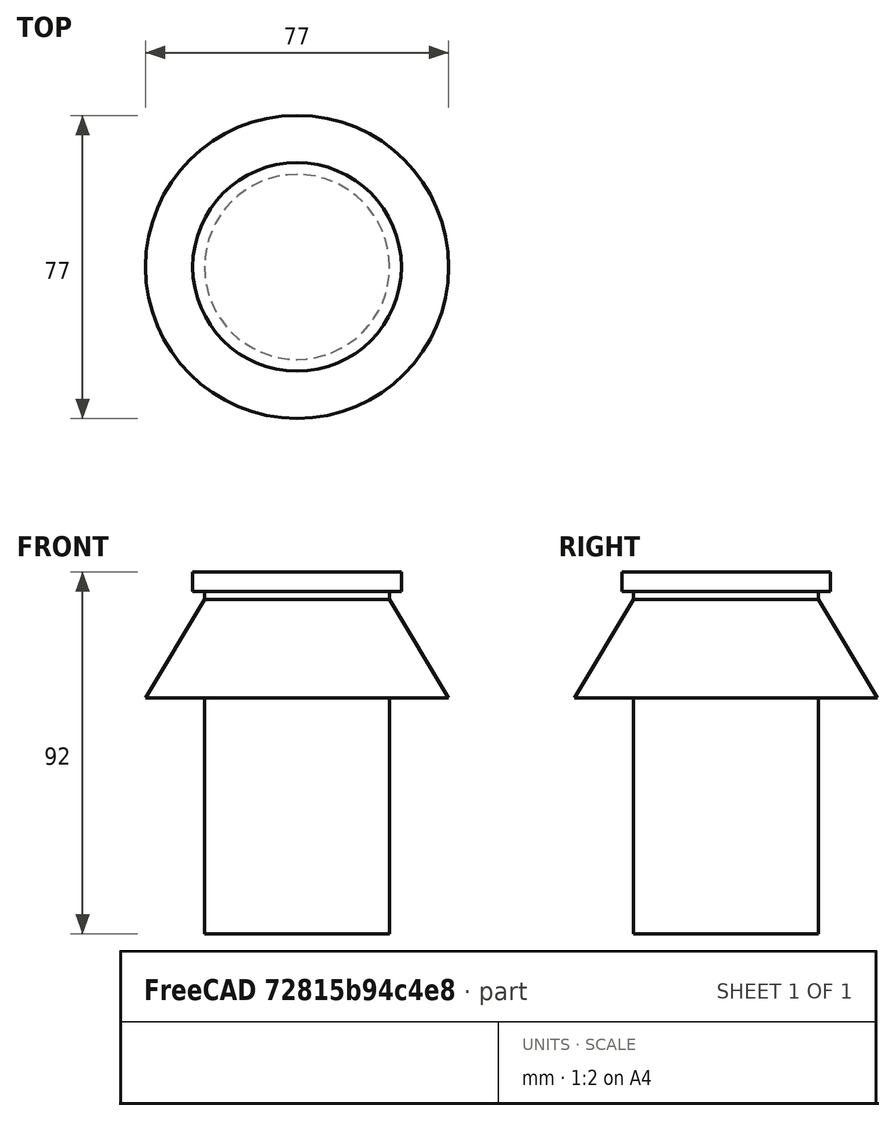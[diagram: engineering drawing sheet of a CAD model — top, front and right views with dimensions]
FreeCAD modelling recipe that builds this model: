
FCSTD DOCUMENT  (FreeCAD 1.1R38898 (Git))
Label: Штамп
License: All rights reserved
LicenseURL: https://en.wikipedia.org/wiki/All_rights_reserved
objects: Sketcher::SketchObject×1, PartDesign::Revolution×1, PartDesign::Body×1
note: 6 computed .brp shape members not serialized (recipe doc carries the construction recipe); baked Part::Feature solids carry a one-line shape summary decoded from their .brp

FEATURE [Sketcher::SketchObject] Sketch
  ArcFitTolerance = 1e-06
  AttachmentSupport = -> [XZ_Plane]
  FullyConstrained = true
  MakeInternals = false
  MapMode = 5
  Placement = pos=(0,0,0) rot=(1,0,0;1.5708rad)
  sketch-geometry (10):
    g0: LineSegment StartX=0 StartY=0 StartZ=0 EndX=-23.5 EndY=0 EndZ=0
    g1: LineSegment StartX=-23.5 StartY=0 StartZ=0 EndX=-23.5 EndY=60 EndZ=0
    g2: LineSegment StartX=-23.5 StartY=60 StartZ=0 EndX=-38.5 EndY=60 EndZ=0
    g3: LineSegment StartX=-38.5 StartY=60 StartZ=0 EndX=-23.5 EndY=85 EndZ=0
    g4: LineSegment StartX=-26.5 StartY=92 StartZ=0 EndX=0 EndY=92 EndZ=0
    g5: LineSegment StartX=0 StartY=92 StartZ=0 EndX=0 EndY=0 EndZ=0
    g6: LineSegment [constr] StartX=-23.5 StartY=60 StartZ=0 EndX=-23.5 EndY=85 EndZ=0
    g7: LineSegment StartX=-23.5 StartY=85 StartZ=0 EndX=-23.5 EndY=87 EndZ=0
    g8: LineSegment StartX=-23.5 StartY=87 StartZ=0 EndX=-26.5 EndY=87 EndZ=0
    g9: LineSegment StartX=-26.5 StartY=87 StartZ=0 EndX=-26.5 EndY=92 EndZ=0
  constraints (28):
    c: Coincident(g-1,g0)
    c: PointOnObject(g0,g-1)
    c: Coincident(g0,g1)
    c: Vertical(g1)
    c: Coincident(g1,g2)
    c: Horizontal(g2)
    c: Coincident(g2,g3)
    c: PointOnObject(g4,g-2)
    c: Coincident(g4,g5)
    c: Coincident(g5,g0)
    c: Horizontal(g4)
    c: DistanceY(g1,g1) = 60
    c: Distance(g2,g2) = 15
    c: Coincident(g6,g1)
    c: DistanceX(g0,g0) = 23.5
    c: DistanceY(g2,g4) = 32
    c: Coincident(g3,g7)
    c: Coincident(g7,g8)
    c: Horizontal(g8)
    c: Coincident(g8,g9)
    c: Vertical(g9)
    c: Coincident(g4,g9)
    c: Coincident(g6,g3)
    c: Distance(g8,g8) = 3
    c: Vertical(g7)
    c: Vertical(g6)
    c: DistanceY(g9,g9) = 5
    c: DistanceY(g3,g3) = 25
FEATURE [PartDesign::Revolution] Revolution
  Angle = 360
  Angle2 = 60
  Axis = (0,2e-16,1)
  Base = (0,0,0)
  Placement = pos=(0,0,0) rot=(1,0,0;1.5708rad)
  Profile = -> Sketch
  ReferenceAxis = -> Sketch [V_Axis]
  Refine = true
  Suppressed = false
  Type = 0
FEATURE [PartDesign::Body] Body  label="Тело"
  AllowCompound = false
  Group = -> [Sketch,Revolution]
  Origin = -> Origin
  Tip = -> Revolution
